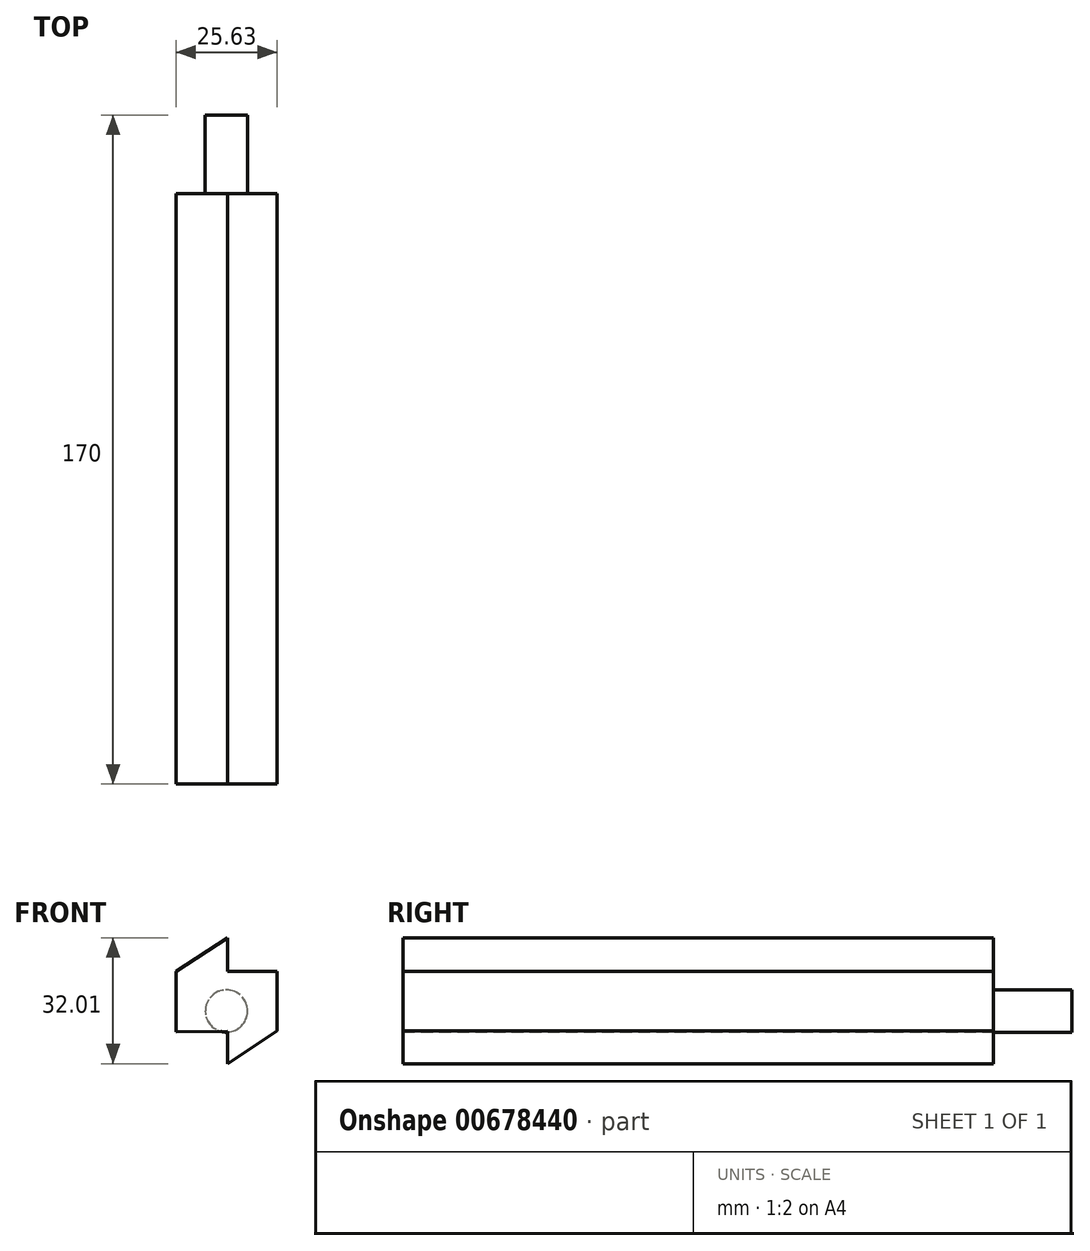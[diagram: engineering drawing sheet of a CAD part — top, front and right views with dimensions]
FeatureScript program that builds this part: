
annotation { "Feature Type Name" : "Feature", "Feature Type Description" : "" }
export const myFeature = defineFeature(function(context is Context, id is Id, definition is map)
    precondition{}
    {
        {
            var Q0;
            Q0=qCreatedBy(makeId("Front.planeOp"),FACE);
            var sketch = newSketch(context, id + "F0", { "sketchPlane" : qUnion([Q0])});
            skLineSegment(sketch, "E0", {"start": v(-12.79, 10.07) * mm, "end": v(-12.79, -5.26) * mm});
            skLineSegment(sketch, "E1", {"start": v(-12.79, 10.07) * mm, "end": v(12.84, 10.07) * mm});
            skLineSegment(sketch, "E2", {"start": v(12.84, 10.07) * mm, "end": v(12.84, -5.07) * mm});
            skLineSegment(sketch, "E3", {"start": v(12.84, -5.07) * mm, "end": v(-12.79, -5.26) * mm});
            skLineSegment(sketch, "E4", {"start": v(-12.79, 10.07) * mm, "end": v(0.32, 18.65) * mm});
            skLineSegment(sketch, "E5", {"start": v(0.32, 18.65) * mm, "end": v(0.32, 10.07) * mm});
            skLineSegment(sketch, "E6", {"start": v(12.84, -5.07) * mm, "end": v(0.32, -13.36) * mm});
            skLineSegment(sketch, "E7", {"start": v(0.32, -13.36) * mm, "end": v(0.26, -5.07) * mm});
            skSolve(sketch);
        }
        {
            var Q0;
            {var subQ3=sQuery(id+"F0.wireOp",EDGE,"E0");Q0=makeQuery(id+"F0.imprint","IMPRINT",FACE,{"disambiguationData":[TD([[makeQuery(id+"F0.imprint","IMPRINT",EDGE,{"derivedFrom":subQ3}),1.0]])]});}
            var Q1;
            {var subQ0=sQuery(id+"F0.wireOp",EDGE,"E4");Q1=makeQuery(id+"F0.imprint","IMPRINT",FACE,{"disambiguationData":[TD([[makeQuery(id+"F0.imprint","IMPRINT",EDGE,{"derivedFrom":subQ0}),-1.0]])]});}
            var Q2;
            {var subQ0=sQuery(id+"F0.wireOp",EDGE,"E6");Q2=makeQuery(id+"F0.imprint","IMPRINT",FACE,{"disambiguationData":[TD([[makeQuery(id+"F0.imprint","IMPRINT",EDGE,{"derivedFrom":subQ0}),-1.0]])]});}
            extrude(context, id + "F1", {"entities" : qUnion([Q0, Q1, Q2]), "depth" : 150 * mm, "offsetDistance" : 25 * mm});
        }
        {
            var Q0;
            Q0=qCreatedBy(makeId("Front.planeOp"),FACE);
            var sketch = newSketch(context, id + "F2", { "sketchPlane" : qUnion([Q0])});
            skCircle(sketch, "E8", {"center": v(0, 0) * mm, "radius": 5.37 * mm});
            skSolve(sketch);
        }
        {
            var Q0;
            Q0=makeQuery(id+"F2.imprint","IMPRINT",FACE,{"disambiguationData":[TD([[makeQuery(id+"F2.imprint","IMPRINT",EDGE,{"derivedFrom":sQuery(id+"F2.wireOp",EDGE,"E8")}),1.0]])]});
            extrude(context, id + "F3", {"entities" : qUnion([Q0]), "operationType" : NewBodyOperationType.ADD, "oppositeDirection" : true, "depth" : 20 * mm, "offsetDistance" : 25 * mm});
        }
    });
